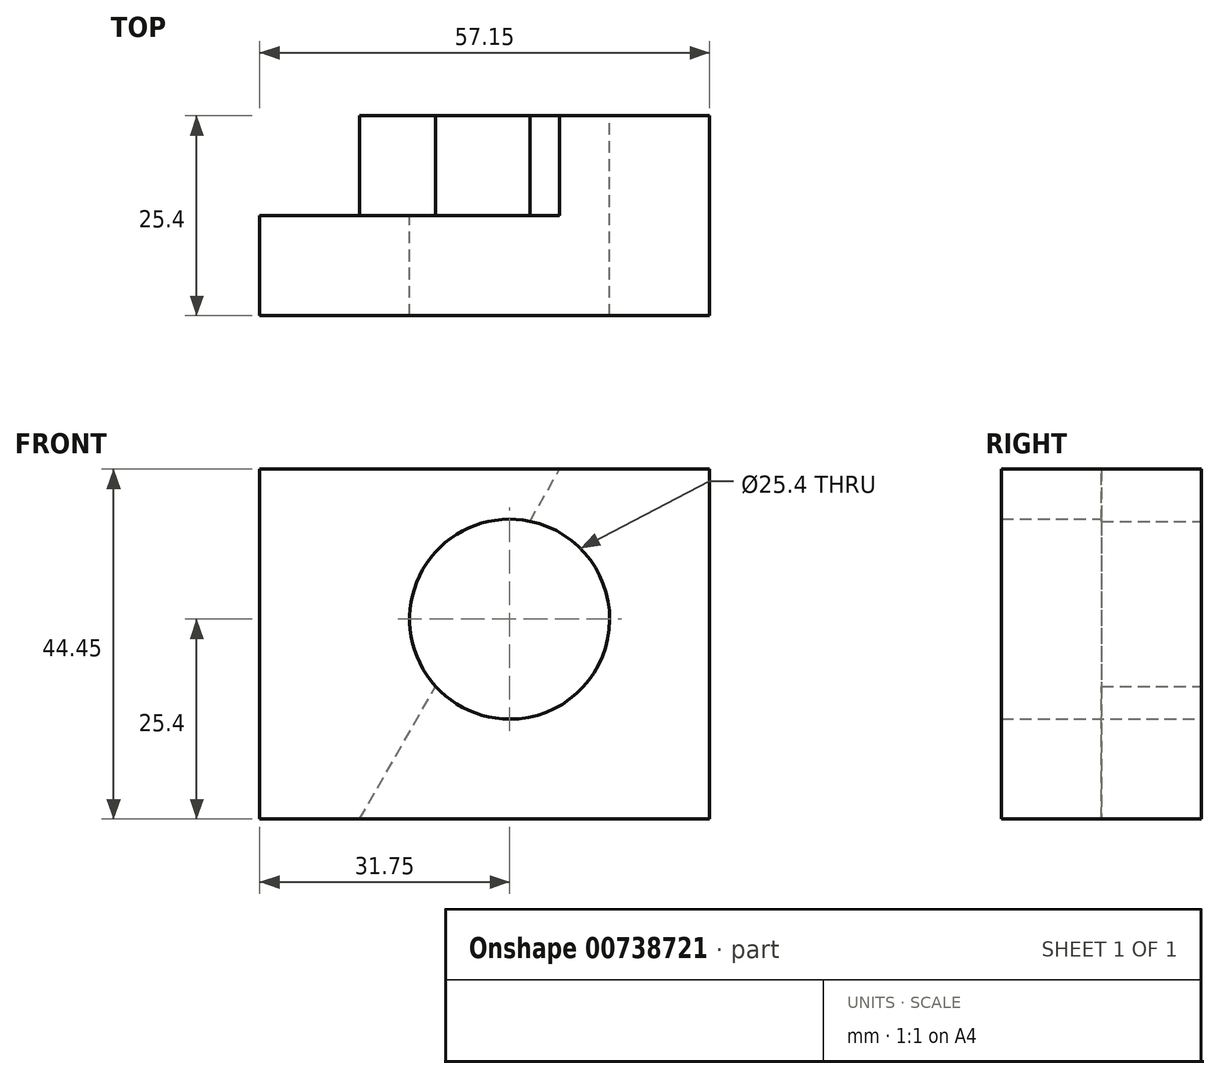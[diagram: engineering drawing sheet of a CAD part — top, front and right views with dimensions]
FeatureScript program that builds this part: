
annotation { "Feature Type Name" : "Feature", "Feature Type Description" : "" }
export const myFeature = defineFeature(function(context is Context, id is Id, definition is map)
    precondition{}
    {
        {
            var Q0;
            Q0=qCreatedBy(makeId("Front.planeOp"),FACE);
            var sketch = newSketch(context, id + "F0", { "sketchPlane" : qUnion([Q0])});
            skLineSegment(sketch, "E0", {"start": v(0, 44.45) * mm, "end": v(0, 0) * mm});
            skLineSegment(sketch, "E1", {"start": v(0, 0) * mm, "end": v(57.15, 0) * mm});
            skLineSegment(sketch, "E2", {"start": v(57.15, 0) * mm, "end": v(57.15, 44.45) * mm});
            skLineSegment(sketch, "E3", {"start": v(57.15, 44.45) * mm, "end": v(0, 44.45) * mm});
            skSolve(sketch);
        }
        {
            var Q0;
            Q0 = qSketchRegion(id + "F0", true);
            extrude(context, id + "F1", {"entities" : qUnion([Q0]), "depth" : 25.4 * mm, "offsetDistance" : 25.4 * mm});
        }
        {
            var Q0;
            Q0=qCreatedBy(makeId("Front.planeOp"),FACE);
            var sketch = newSketch(context, id + "F2", { "sketchPlane" : qUnion([Q0])});
            skLineSegment(sketch, "E4", {"start": v(12.7, 0) * mm, "end": v(38.1, 44.45) * mm});
            skLineSegment(sketch, "E5", {"start": v(38.1, 44.45) * mm, "end": v(0, 44.45) * mm});
            skLineSegment(sketch, "E6", {"start": v(0, 44.45) * mm, "end": v(0, 0) * mm});
            skLineSegment(sketch, "E7", {"start": v(0, 0) * mm, "end": v(12.7, 0) * mm});
            skSolve(sketch);
        }
        {
            var Q0;
            Q0 = qSketchRegion(id + "F2", true);
            extrude(context, id + "F3", {"entities" : qUnion([Q0]), "operationType" : NewBodyOperationType.REMOVE, "depth" : 12.7 * mm, "offsetDistance" : 25.4 * mm});
        }
        {
            var Q0;
            Q0=qCreatedBy(makeId("Front.planeOp"),FACE);
            var sketch = newSketch(context, id + "F4", { "sketchPlane" : qUnion([Q0])});
            skCircle(sketch, "E8", {"center": v(31.75, 25.4) * mm, "radius": 12.7 * mm});
            skSolve(sketch);
        }
        {
            var Q0;
            Q0 = qSketchRegion(id + "F4", true);
            extrude(context, id + "F5", {"entities" : qUnion([Q0]), "operationType" : NewBodyOperationType.REMOVE, "endBound" : BoundingType.THROUGH_ALL, "depth" : 25.4 * mm, "offsetDistance" : 25.4 * mm});
        }
    });
